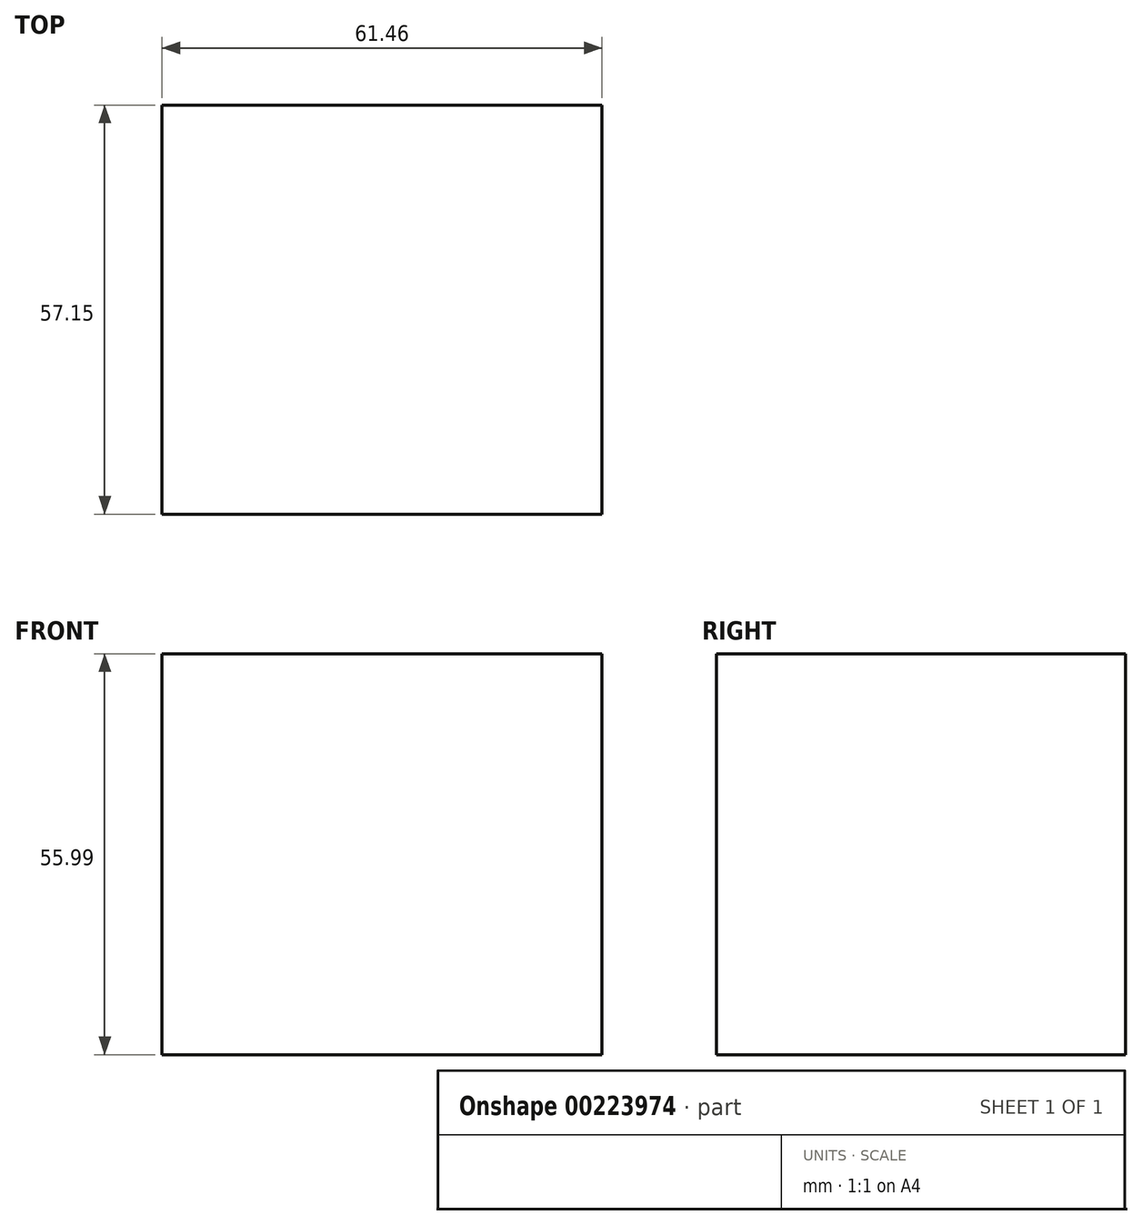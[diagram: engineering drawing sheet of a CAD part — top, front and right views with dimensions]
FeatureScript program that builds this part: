
annotation { "Feature Type Name" : "Feature", "Feature Type Description" : "" }
export const myFeature = defineFeature(function(context is Context, id is Id, definition is map)
    precondition{}
    {
        {
            var Q0;
            Q0=qCreatedBy(makeId("Front.planeOp"),FACE);
            var sketch = newSketch(context, id + "F0", { "sketchPlane" : qUnion([Q0])});
            skLineSegment(sketch, "E0.bottom", {"start": v(-19.77, -13.87) * mm, "end": v(41.69, -13.87) * mm});
            skLineSegment(sketch, "E0.top", {"start": v(-19.77, 42.12) * mm, "end": v(41.69, 42.12) * mm});
            skLineSegment(sketch, "E0.left", {"start": v(-19.77, -13.87) * mm, "end": v(-19.77, 42.12) * mm});
            skLineSegment(sketch, "E0.right", {"start": v(41.69, -13.87) * mm, "end": v(41.69, 42.12) * mm});
            skSolve(sketch);
        }
        {
            var Q0;
            Q0=makeQuery(id+"F0.imprint","IMPRINT",FACE,{"disambiguationData":[TD([[makeQuery(id+"F0.imprint","IMPRINT",EDGE,{"derivedFrom":sQuery(id+"F0.wireOp",EDGE,"E0.bottom")}),1.0]])]});
            extrude(context, id + "F1", {"entities" : qUnion([Q0]), "depth" : 57.15 * mm});
        }
    });
